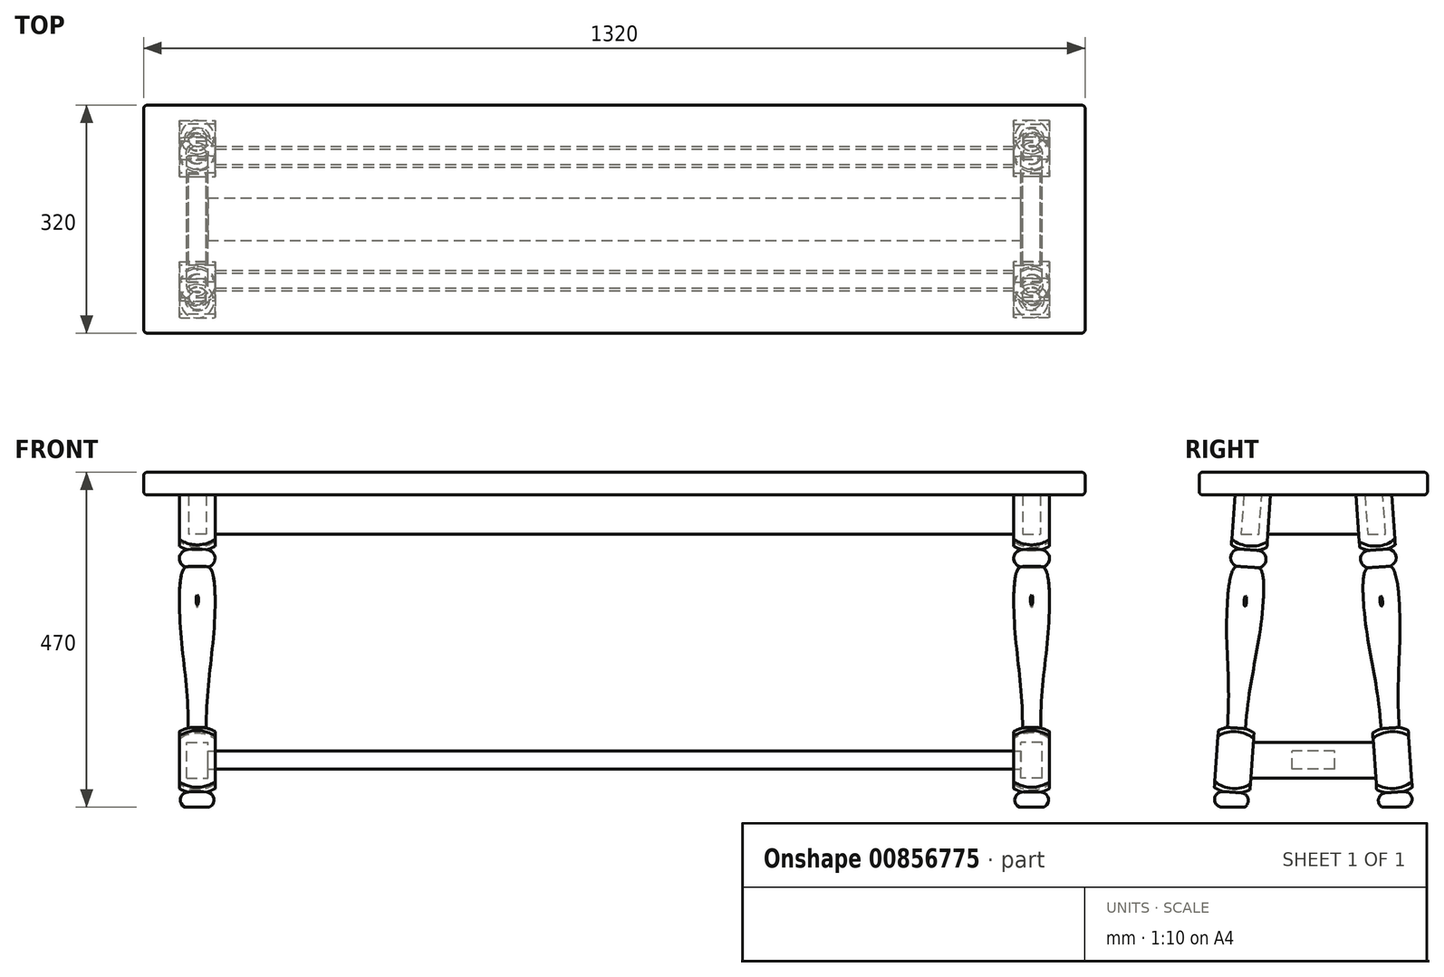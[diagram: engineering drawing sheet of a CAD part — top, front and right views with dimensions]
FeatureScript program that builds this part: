
annotation { "Feature Type Name" : "Feature", "Feature Type Description" : "" }
export const myFeature = defineFeature(function(context is Context, id is Id, definition is map)
    precondition{}
    {
        {
            assignVariable(context, id + "F0", {"name" : "height", "anyValue" : 470});
        }
        {
            assignVariable(context, id + "F1", {"name" : "topThick", "anyValue" : 32});
        }
        {
            assignVariable(context, id + "F2", {"name" : "endOverhang", "anyValue" : 75});
        }
        {
            assignVariable(context, id + "F3", {"name" : "legThick", "anyValue" : 50});
        }
        {
            var Q0;
            Q0=qCreatedBy(makeId("Top.planeOp"),FACE);
            cPlane(context, id + "F4", {"entities" : qUnion([Q0]), "cplaneType" : CPlaneType.OFFSET, "offset" : (getVariable(context, 'height')) * mm, "width" : 150 * mm, "height" : 150 * mm});
        }
        {
            var Q0;
            Q0=qCreatedBy(id+"F4.planeOp",FACE);
            var sketch = newSketch(context, id + "F5", { "sketchPlane" : qUnion([Q0])});
            skLineSegment(sketch, "E0.bottom", {"start": v(660, 160) * mm, "end": v(-660, 160) * mm});
            skLineSegment(sketch, "E0.top", {"start": v(660, -160) * mm, "end": v(-660, -160) * mm});
            skLineSegment(sketch, "E0.left", {"start": v(660, 160) * mm, "end": v(660, -160) * mm});
            skLineSegment(sketch, "E0.right", {"start": v(-660, 160) * mm, "end": v(-660, -160) * mm});
            skPoint(sketch, "E0.middle", {"position": v(0, 0) * mm});
            skSolve(sketch);
        }
        {
            var Q0;
            Q0=qSketchRegion(id+"F5",true);
            extrude(context, id + "F6", {"entities" : qUnion([Q0]), "oppositeDirection" : true, "depth" : (getVariable(context, 'topThick')) * mm, "offsetDistance" : 25 * mm});
        }
        {
            var Q0;
            Q0=makeQuery(id+"F6.opExtrude","SWEPT_FACE",FACE,{"disambiguationData":[OSD([sQuery(id+"F5.wireOp",EDGE,"E0.left")])]});
            cPlane(context, id + "F7", {"entities" : qUnion([Q0]), "cplaneType" : CPlaneType.OFFSET, "offset" : (getVariable(context, 'endOverhang')) * mm, "oppositeDirection" : true, "width" : 150 * mm, "height" : 150 * mm});
        }
        {
            var Q0;
            Q0=qCreatedBy(id+"F7.planeOp",FACE);
            var sketch = newSketch(context, id + "F8", { "sketchPlane" : qUnion([Q0])});
            skLineSegment(sketch, "E1", {"start": v(-110, 438) * mm, "end": v(-140.63, 0) * mm});
            skLineSegment(sketch, "E2", {"start": v(-140.63, 0) * mm, "end": v(-90.5, 0) * mm});
            skLineSegment(sketch, "E3", {"start": v(-90.5, 0) * mm, "end": v(-59.88, 438) * mm});
            skLineSegment(sketch, "E4", {"start": v(-59.88, 438) * mm, "end": v(-110, 438) * mm});
            skLineSegment(sketch, "E5", {"start": v(-59.88, 438) * mm, "end": v(-59.88, 337.58) * mm, "construction": true});
            skSolve(sketch);
        }
        {
            var Q0;
            Q0=makeQuery(id+"F8.imprint","IMPRINT",FACE,{"disambiguationData":[TD([[makeQuery(id+"F8.imprint","IMPRINT",EDGE,{"derivedFrom":sQuery(id+"F8.wireOp",EDGE,"E1")}),1.0]])]});
            extrude(context, id + "F9", {"entities" : qUnion([Q0]), "endBound" : BoundingType.SYMMETRIC, "depth" : (getVariable(context, 'legThick')) * mm, "offsetDistance" : 25 * mm});
        }
        {
            var Q0;
            Q0=qCreatedBy(id+"F7.planeOp",FACE);
            var sketch = newSketch(context, id + "F10", { "sketchPlane" : qUnion([Q0])});
            skPoint(sketch, "E6.0", {"position": v(-115.57, 0) * mm});
            skLineSegment(sketch, "E7.0.1", {"start": v(-160, 470) * mm, "end": v(-160, 438) * mm, "construction": true});
            skLineSegment(sketch, "E7.0.2", {"start": v(-160, 438) * mm, "end": v(160, 438) * mm, "construction": true});
            skPoint(sketch, "E8.0", {"position": v(-84.94, 438) * mm});
            skLineSegment(sketch, "E9", {"start": v(-84.94, 438) * mm, "end": v(-115.57, 0) * mm, "construction": true});
            skLineSegment(sketch, "E10", {"start": v(-72.84, 428.95) * mm, "end": v(-102.84, 0) * mm, "construction": true});
            skPoint(sketch, "E11", {"position": v(-114.9, 368) * mm});
            skLineSegment(sketch, "E12", {"start": v(-97.67, 438) * mm, "end": v(-128.3, 0) * mm, "construction": true});
            skArc(sketch, "E13", {"start": v(-126.76, 21.95) * mm, "mid": v(-138.5, 11.74) * mm, "end": v(-128.3, 0) * mm});
            skLineSegment(sketch, "E14", {"start": v(-128.3, 0) * mm, "end": v(-126.76, 21.95) * mm, "construction": true});
            skArc(sketch, "E15", {"start": v(-152.63, 42.03) * mm, "mid": v(-141.39, 29.81) * mm, "end": v(-126.76, 21.95) * mm});
            skLineSegment(sketch, "E16", {"start": v(-152.63, 42.03) * mm, "end": v(-155.57, 0) * mm});
            skLineSegment(sketch, "E17", {"start": v(-155.57, 0) * mm, "end": v(-128.3, 0) * mm});
            skLineSegment(sketch, "E18", {"start": v(-128.3, 0) * mm, "end": v(-128.3, 0) * mm});
            skPoint(sketch, "E19", {"position": v(-138.68, 27.85) * mm});
            skPoint(sketch, "E20", {"position": v(-133.1, 107.66) * mm});
            skArc(sketch, "E21", {"start": v(-102.98, 362.1) * mm, "mid": v(-117.6, 369.96) * mm, "end": v(-128.84, 382.18) * mm});
            skArc(sketch, "E22", {"start": v(-102.98, 362.1) * mm, "mid": v(-116.1, 350.68) * mm, "end": v(-104.7, 337.56) * mm});
            skArc(sketch, "E23", {"start": v(-120.48, 111.84) * mm, "mid": v(-136.05, 106.1) * mm, "end": v(-148.88, 95.56) * mm});
            skFitSpline(sketch, "E24", {"points": [v(-107.32, 338.03) * mm, v(-120.78, 283.78) * mm, v(-120.1, 201.24) * mm, v(-120.48, 111.84) * mm], "startDerivative": vector(-91.7, -14.85) * mm, "endDerivative": vector(-21.4, -305.94) * mm});
            skLineSegment(sketch, "E25", {"start": v(-128.84, 382.18) * mm, "end": v(-148.88, 95.56) * mm});
            skSolve(sketch);
        }
        {
            var Q0;
            Q0=qSketchRegion(id+"F10",true);
            var Q1;
            Q1=sQuery(id+"F10.wireOp",EDGE,"E9");
            revolve(context, id + "F11", {"operationType" : NewBodyOperationType.REMOVE, "surfaceOperationType" : NewSurfaceOperationType.NEW, "entities" : qUnion([Q0]), "axis" : qUnion([Q1]), "revolveType" : RevolveType.FULL, "oppositeDirection" : true});
        }
        {
            var Q0;
            Q0=makeQuery(id+"F9.opExtrude","SWEPT_BODY",BODY,{"disambiguationData":[OSD([sQuery(id+"F8.wireOp",EDGE,"E1"),sQuery(id+"F8.wireOp",EDGE,"E2"),sQuery(id+"F8.wireOp",EDGE,"E3"),sQuery(id+"F8.wireOp",EDGE,"E4")])]});
            var Q1;
            Q1=qCreatedBy(makeId("Front.planeOp"),FACE);
            mirror(context, id + "F12", {"entities" : qUnion([Q0]), "mirrorPlane" : qUnion([Q1])});
        }
        {
            var Q0;
            Q0=qCreatedBy(makeId("Front.planeOp"),FACE);
            var sketch = newSketch(context, id + "F13", { "sketchPlane" : qUnion([Q0])});
            skLineSegment(sketch, "E26.bottom", {"start": v(572.5, 438) * mm, "end": v(597.5, 438) * mm});
            skLineSegment(sketch, "E26.top", {"start": v(572.5, 383) * mm, "end": v(597.5, 383) * mm});
            skLineSegment(sketch, "E26.left", {"start": v(572.5, 438) * mm, "end": v(572.5, 383) * mm});
            skLineSegment(sketch, "E26.right", {"start": v(597.5, 438) * mm, "end": v(597.5, 383) * mm});
            skPoint(sketch, "E27.0", {"position": v(560, 35.78) * mm});
            skLineSegment(sketch, "E28", {"start": v(572.5, 66) * mm, "end": v(597.5, 66) * mm, "construction": true});
            skLineSegment(sketch, "E29", {"start": v(585, 98.35) * mm, "end": v(585, 33.22) * mm, "construction": true});
            skLineSegment(sketch, "E30.bottom", {"start": v(600, 41) * mm, "end": v(570, 41) * mm});
            skLineSegment(sketch, "E30.top", {"start": v(600, 91) * mm, "end": v(570, 91) * mm});
            skLineSegment(sketch, "E30.left", {"start": v(600, 41) * mm, "end": v(600, 91) * mm});
            skLineSegment(sketch, "E30.right", {"start": v(570, 41) * mm, "end": v(570, 91) * mm});
            skPoint(sketch, "E31", {"position": v(560, 96.24) * mm});
            skSolve(sketch);
        }
        {
            var Q0;
            Q0=qSketchRegion(id+"F13",true);
            extrude(context, id + "F14", {"entities" : qUnion([Q0]), "endBound" : BoundingType.UP_TO_NEXT, "depth" : 25 * mm, "offsetDistance" : 25 * mm, "hasSecondDirection" : true, "secondDirectionBound" : SecondDirectionBoundingType.UP_TO_NEXT, "secondDirectionOppositeDirection" : true, "secondDirectionDepth" : 25 * mm});
        }
        {
            var Q0;
            Q0=makeQuery(id+"F9.opExtrude","SWEPT_BODY",BODY,{"disambiguationData":[OSD([sQuery(id+"F8.wireOp",EDGE,"E1"),sQuery(id+"F8.wireOp",EDGE,"E2"),sQuery(id+"F8.wireOp",EDGE,"E3"),sQuery(id+"F8.wireOp",EDGE,"E4")])]});
            var Q1;
            Q1=makeQuery(id+"F12.opPattern","COPY",BODY,{"derivedFrom":makeQuery(id+"F9.opExtrude","SWEPT_BODY",BODY,{"disambiguationData":[OSD([sQuery(id+"F8.wireOp",EDGE,"E1"),sQuery(id+"F8.wireOp",EDGE,"E2"),sQuery(id+"F8.wireOp",EDGE,"E3"),sQuery(id+"F8.wireOp",EDGE,"E4")])]}),"instanceName":"1"});
            var Q2;
            Q2=makeQuery(id+"F14.opExtrude","SWEPT_BODY",BODY,{"disambiguationData":[OSD([sQuery(id+"F13.wireOp",EDGE,"E26.bottom"),sQuery(id+"F13.wireOp",EDGE,"E26.top"),sQuery(id+"F13.wireOp",EDGE,"E26.left"),sQuery(id+"F13.wireOp",EDGE,"E26.right")])]});
            var Q3;
            Q3=makeQuery(id+"F14.opExtrude","SWEPT_BODY",BODY,{"disambiguationData":[OSD([sQuery(id+"F13.wireOp",EDGE,"BnCIRoV5-ClaH-NYET-GIcL-QBvj8xOGhHcY.bottom"),sQuery(id+"F13.wireOp",EDGE,"BnCIRoV5-ClaH-NYET-GIcL-QBvj8xOGhHcY.top"),sQuery(id+"F13.wireOp",EDGE,"BnCIRoV5-ClaH-NYET-GIcL-QBvj8xOGhHcY.left"),sQuery(id+"F13.wireOp",EDGE,"BnCIRoV5-ClaH-NYET-GIcL-QBvj8xOGhHcY.right")])]});
            var Q4;
            Q4=makeQuery(id+"F14.opExtrude","SWEPT_BODY",BODY,{"disambiguationData":[OSD([sQuery(id+"F13.wireOp",EDGE,"E30.bottom"),sQuery(id+"F13.wireOp",EDGE,"E30.top"),sQuery(id+"F13.wireOp",EDGE,"E30.left"),sQuery(id+"F13.wireOp",EDGE,"E30.right")])]});
            var Q5;
            Q5=qCreatedBy(makeId("Right.planeOp"),FACE);
            mirror(context, id + "F15", {"entities" : qUnion([Q0, Q1, Q2, Q3, Q4]), "mirrorPlane" : qUnion([Q5])});
        }
        {
            var Q0;
            Q0=qCreatedBy(makeId("Right.planeOp"),FACE);
            var sketch = newSketch(context, id + "F16", { "sketchPlane" : qUnion([Q0])});
            skLineSegment(sketch, "E32.bottom", {"start": v(-30, 78.5) * mm, "end": v(30, 78.5) * mm});
            skLineSegment(sketch, "E32.top", {"start": v(-30, 53.5) * mm, "end": v(30, 53.5) * mm});
            skLineSegment(sketch, "E32.left", {"start": v(-30, 78.5) * mm, "end": v(-30, 53.5) * mm});
            skLineSegment(sketch, "E32.right", {"start": v(30, 78.5) * mm, "end": v(30, 53.5) * mm});
            skLineSegment(sketch, "E33", {"start": v(-30, 66) * mm, "end": v(30, 66) * mm, "construction": true});
            skLineSegment(sketch, "E34", {"start": v(-97.47, 438) * mm, "end": v(-101.32, 383) * mm});
            skLineSegment(sketch, "E35", {"start": v(-101.32, 383) * mm, "end": v(-76.25, 383) * mm});
            skLineSegment(sketch, "E36", {"start": v(-76.25, 383) * mm, "end": v(-72.4, 438) * mm});
            skLineSegment(sketch, "E37", {"start": v(-72.4, 438) * mm, "end": v(-97.47, 438) * mm});
            skLineSegment(sketch, "E38", {"start": v(-84.94, 438) * mm, "end": v(-88.78, 383) * mm, "construction": true});
            skLineSegment(sketch, "E39.MirrorCS", {"start": v(72.4, 438) * mm, "end": v(97.47, 438) * mm});
            skLineSegment(sketch, "E40.MirrorCS", {"start": v(101.32, 383) * mm, "end": v(76.25, 383) * mm});
            skLineSegment(sketch, "E41.MirrorCS", {"start": v(76.25, 383) * mm, "end": v(72.4, 438) * mm});
            skLineSegment(sketch, "E42.MirrorCS", {"start": v(84.94, 438) * mm, "end": v(88.78, 383) * mm, "construction": true});
            skLineSegment(sketch, "E43.MirrorCS", {"start": v(97.47, 438) * mm, "end": v(101.32, 383) * mm});
            skSolve(sketch);
        }
        {
            var Q0;
            Q0=makeQuery(id+"F16.imprint","IMPRINT",FACE,{"disambiguationData":[TD([[makeQuery(id+"F16.imprint","IMPRINT",EDGE,{"derivedFrom":sQuery(id+"F16.wireOp",EDGE,"E34")}),1.0]])]});
            var Q1;
            Q1=makeQuery(id+"F16.imprint","IMPRINT",FACE,{"disambiguationData":[TD([[makeQuery(id+"F16.imprint","IMPRINT",EDGE,{"derivedFrom":sQuery(id+"F16.wireOp",EDGE,"E39.MirrorCS")}),-1.0]])]});
            var Q2;
            {var subQ0=sQuery(id+"F8.wireOp",EDGE,"E1");var subQ1=sQuery(id+"F8.wireOp",EDGE,"E4");var subQ2=sQuery(id+"F8.wireOp",EDGE,"E3");Q2=makeQuery(id+"F11.boolean.opBoolean","SPLIT",FACE,{"disambiguationData":[TD([makeQuery(id+"F9.opExtrude","SWEPT_FACE",FACE,{"disambiguationData":[OSD([subQ1])]})])],"derivedFrom":makeQuery(id+"F9.opExtrude","CAP_FACE",FACE,{"disambiguationData":[OSD([subQ0,sQuery(id+"F8.wireOp",EDGE,"E2"),subQ2,subQ1])],"isStart":true})});}
            var Q3;
            Q3=makeQuery(id+"F9.opExtrude","SWEPT_BODY",BODY,{"disambiguationData":[OSD([sQuery(id+"F8.wireOp",EDGE,"E1"),sQuery(id+"F8.wireOp",EDGE,"E2"),sQuery(id+"F8.wireOp",EDGE,"E3"),sQuery(id+"F8.wireOp",EDGE,"E4")])]});
            var Q4;
            {var subQ0=sQuery(id+"F8.wireOp",EDGE,"E1");var subQ1=sQuery(id+"F8.wireOp",EDGE,"E4");var subQ2=sQuery(id+"F8.wireOp",EDGE,"E3");Q4=makeQuery(id+"F15.opPattern","COPY",FACE,{"derivedFrom":makeQuery(id+"F11.boolean.opBoolean","SPLIT",FACE,{"disambiguationData":[TD([makeQuery(id+"F9.opExtrude","SWEPT_FACE",FACE,{"disambiguationData":[OSD([subQ1])]})])],"derivedFrom":makeQuery(id+"F9.opExtrude","CAP_FACE",FACE,{"disambiguationData":[OSD([subQ0,sQuery(id+"F8.wireOp",EDGE,"E2"),subQ2,subQ1])],"isStart":true})}),"instanceName":"1"});}
            extrude(context, id + "F17", {"entities" : qUnion([Q0, Q1]), "endBound" : BoundingType.UP_TO_SURFACE, "depth" : 25 * mm, "endBoundEntityFace" : qUnion([Q2]), "endBoundEntityBody" : qUnion([Q3]), "offsetDistance" : 25 * mm, "hasSecondDirection" : true, "secondDirectionBound" : SecondDirectionBoundingType.UP_TO_SURFACE, "secondDirectionOppositeDirection" : true, "secondDirectionDepth" : 25 * mm, "secondDirectionBoundEntityFace" : qUnion([Q4])});
        }
        {
            var Q0;
            Q0=makeQuery(id+"F16.imprint","IMPRINT",FACE,{"disambiguationData":[TD([[makeQuery(id+"F16.imprint","IMPRINT",EDGE,{"derivedFrom":sQuery(id+"F16.wireOp",EDGE,"E32.bottom")}),-1.0]])]});
            var Q1;
            Q1=makeQuery(id+"F15.opPattern","COPY",FACE,{"derivedFrom":makeQuery(id+"F14.opExtrude","SWEPT_FACE",FACE,{"disambiguationData":[OSD([sQuery(id+"F13.wireOp",EDGE,"E30.right")])]}),"instanceName":"1"});
            var Q2;
            Q2=makeQuery(id+"F14.opExtrude","SWEPT_FACE",FACE,{"disambiguationData":[OSD([sQuery(id+"F13.wireOp",EDGE,"E30.right")])]});
            extrude(context, id + "F18", {"entities" : qUnion([Q0]), "endBound" : BoundingType.UP_TO_SURFACE, "oppositeDirection" : true, "depth" : 25 * mm, "endBoundEntityFace" : qUnion([Q1]), "offsetDistance" : 25 * mm, "hasSecondDirection" : true, "secondDirectionBound" : SecondDirectionBoundingType.UP_TO_SURFACE, "secondDirectionOppositeDirection" : false, "secondDirectionDepth" : 25 * mm, "secondDirectionBoundEntityFace" : qUnion([Q2])});
        }
        {
            var Q0;
            Q0=makeQuery(id+"F6.opExtrude","CAP_FACE",FACE,{"disambiguationData":[OSD([sQuery(id+"F5.wireOp",EDGE,"E0.bottom"),sQuery(id+"F5.wireOp",EDGE,"E0.top"),sQuery(id+"F5.wireOp",EDGE,"E0.left"),sQuery(id+"F5.wireOp",EDGE,"E0.right")])],"isStart":true});
            var Q1;
            Q1=makeQuery(id+"F6.opExtrude","SWEPT_FACE",FACE,{"disambiguationData":[OSD([sQuery(id+"F5.wireOp",EDGE,"E0.left")])]});
            var Q2;
            Q2=makeQuery(id+"F6.opExtrude","SWEPT_FACE",FACE,{"disambiguationData":[OSD([sQuery(id+"F5.wireOp",EDGE,"E0.right")])]});
            var Q3;
            Q3=makeQuery(id+"F6.opExtrude","CAP_FACE",FACE,{"disambiguationData":[OSD([sQuery(id+"F5.wireOp",EDGE,"E0.bottom"),sQuery(id+"F5.wireOp",EDGE,"E0.top"),sQuery(id+"F5.wireOp",EDGE,"E0.left"),sQuery(id+"F5.wireOp",EDGE,"E0.right")])],"isStart":false});
            fillet(context, id + "F19", {"entities" : qUnion([Q0, Q1, Q2, Q3]), "radius" : 5 * mm, "tangentPropagation" : true, "allowEdgeOverflow" : false});
        }
    });
